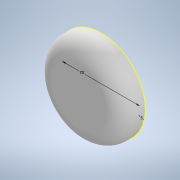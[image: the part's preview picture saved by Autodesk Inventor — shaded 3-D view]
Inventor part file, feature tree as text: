
AUTODESK INVENTOR PART (.ipt)
format: ipt  version: 2020.2 (Build 242310000, 310)  size: 173,568 bytes
history: native  units: in
note: dims shown in document units (in); Inventor stores cm internally (conversion verified against a paired STEP export)
features: sketch x4, revolve x1, fillet x1, extrude x1, other x1, pattern_circular x1
ambient origin geometry x8: Origin, YZ Plane, XZ Plane, XY Plane, X Axis, Y Axis, Z Axis, Center Point
bodies: Solid1 (feature_tree)
feature tree (9):
  revolve  "Revolution1"  [1 undecoded]
  fillet  "Fillet1"  [1 undecoded]
  sketch  "Sketch2"  dims[d3=0.5906in d4=2.7559in]
  extrude  "Extrusion1"  Depth=2.7559in
  sketch  "Sketch4"  dims[d6=0.1181in d7=0.1181in d14=0.3937in d15=0.1969in d16=0.1969in d17=1.2783in d18=0.7874in d19=0.0in d20=3.1496in d21=3.1496in d22=1.1811in d23=360.0deg]
  other  "Work Axis1"
  pattern_circular  "Circular Pattern1"  [2 undecoded]
  sketch  "Sketch1"  dims[d0=1.5748in d1=0.7874in d2=90.0deg]
  sketch  "Sketch3"  dims[d5=0.1969in]
note: 4 required parameter values undecoded (feature->parameter linkage not recoverable at this tier; creation-order binding heuristic only, values carry confidence <= 0.55)